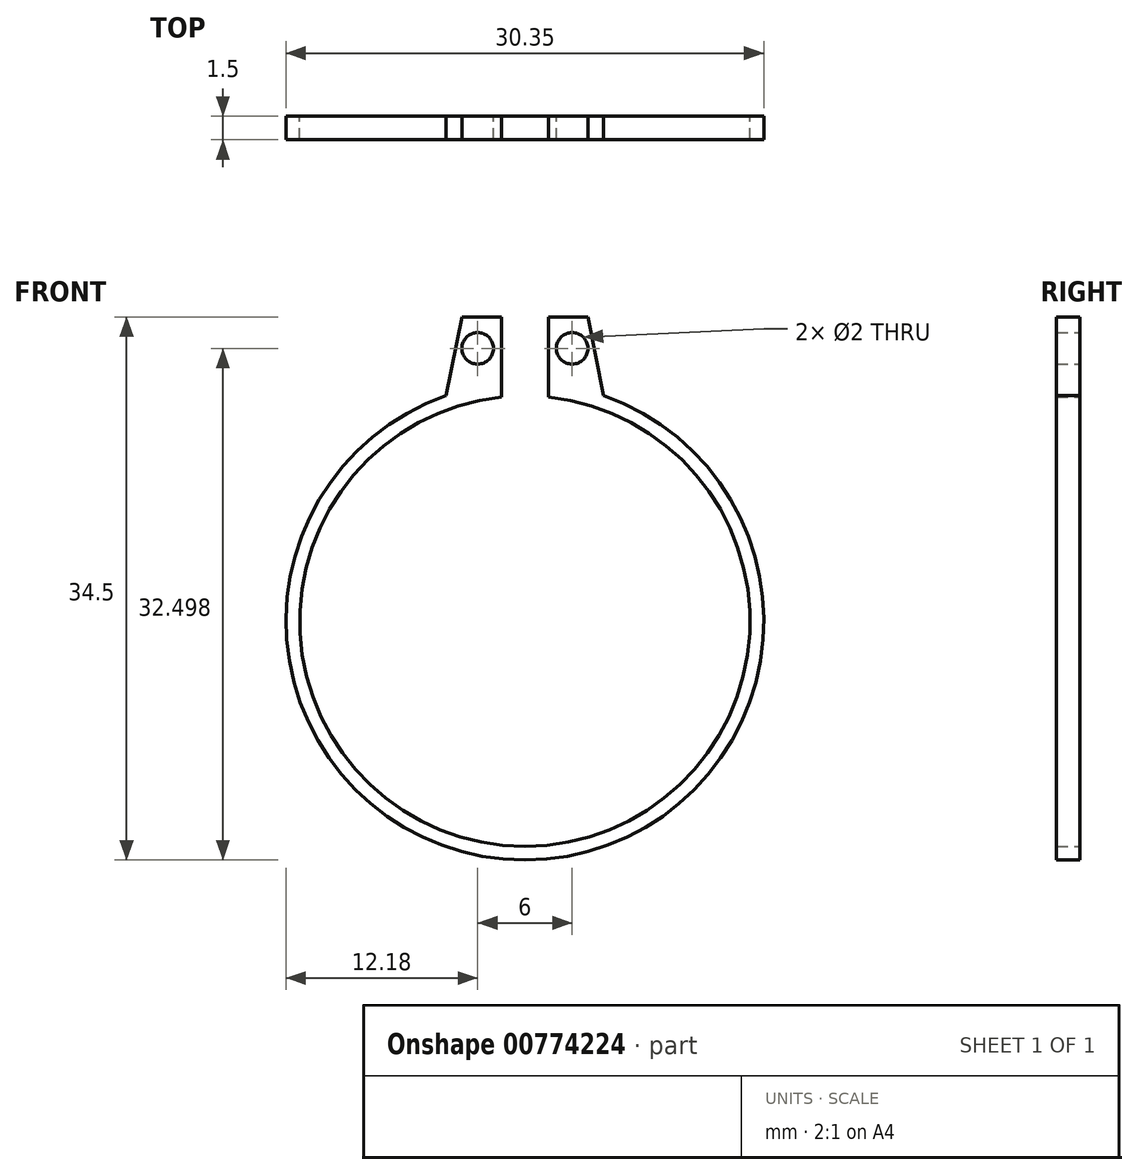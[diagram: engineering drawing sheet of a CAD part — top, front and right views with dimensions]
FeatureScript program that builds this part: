
annotation { "Feature Type Name" : "Feature", "Feature Type Description" : "" }
export const myFeature = defineFeature(function(context is Context, id is Id, definition is map)
    precondition{}
    {
        {
            var Q0;
            Q0=qCreatedBy(makeId("Front.planeOp"),FACE);
            var sketch = newSketch(context, id + "F0", { "sketchPlane" : qUnion([Q0])});
            skCircle(sketch, "E0", {"center": v(0, 0) * mm, "radius": 14.3 * mm});
            skCircle(sketch, "E1", {"center": v(0, 0) * mm, "radius": 15.18 * mm});
            skLineSegment(sketch, "E2", {"start": v(-5, 14.33) * mm, "end": v(-4, 19.33) * mm});
            skLineSegment(sketch, "E3", {"start": v(-4, 19.33) * mm, "end": v(0, 19.33) * mm});
            skLineSegment(sketch, "E4", {"start": v(0, 19.33) * mm, "end": v(4, 19.33) * mm});
            skLineSegment(sketch, "E5", {"start": v(4, 19.33) * mm, "end": v(5, 14.33) * mm});
            skLineSegment(sketch, "E6", {"start": v(5, 14.33) * mm, "end": v(-5, 14.33) * mm});
            skCircle(sketch, "E7", {"center": v(-3, 17.33) * mm, "radius": 1 * mm});
            skCircle(sketch, "E8", {"center": v(3, 17.33) * mm, "radius": 1 * mm});
            skSolve(sketch);
        }
        {
            var Q0;
            Q0 = qSketchRegion(id + "F0", true);
            extrude(context, id + "F1", {"entities" : qUnion([Q0]), "depth" : 1.5 * mm, "offsetDistance" : 25 * mm});
        }
        {
            var Q0;
            Q0=makeQuery(id+"F1.opExtrude","CAP_FACE",FACE,{"disambiguationData":[OSD([sQuery(id+"F0.wireOp",EDGE,"E0"),sQuery(id+"F0.wireOp",EDGE,"E1"),sQuery(id+"F0.wireOp",EDGE,"E2"),sQuery(id+"F0.wireOp",EDGE,"E3"),sQuery(id+"F0.wireOp",EDGE,"E4"),sQuery(id+"F0.wireOp",EDGE,"E5"),sQuery(id+"F0.wireOp",EDGE,"E7"),sQuery(id+"F0.wireOp",EDGE,"E8")])],"isStart":false});
            var sketch = newSketch(context, id + "F2", { "sketchPlane" : qUnion([Q0])});
            skLineSegment(sketch, "E9.bottom", {"start": v(-1.5, 30) * mm, "end": v(1.5, 30) * mm});
            skLineSegment(sketch, "E9.top", {"start": v(-1.5, 0) * mm, "end": v(1.5, 0) * mm});
            skLineSegment(sketch, "E9.left", {"start": v(-1.5, 30) * mm, "end": v(-1.5, 0) * mm});
            skLineSegment(sketch, "E9.right", {"start": v(1.5, 30) * mm, "end": v(1.5, 0) * mm});
            skSolve(sketch);
        }
        {
            var Q0;
            Q0 = qSketchRegion(id + "F2", true);
            extrude(context, id + "F3", {"entities" : qUnion([Q0]), "operationType" : NewBodyOperationType.REMOVE, "endBound" : BoundingType.THROUGH_ALL, "oppositeDirection" : true, "depth" : 25 * mm, "offsetDistance" : 25 * mm});
        }
    });
